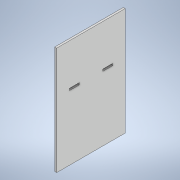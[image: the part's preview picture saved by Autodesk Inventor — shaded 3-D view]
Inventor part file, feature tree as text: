
AUTODESK INVENTOR PART (.ipt)
format: ipt  version: 2020 (Build 240168000, 168)  size: 120,832 bytes
history: native  units: mm
features: extrude x2, sketch x2
ambient origin geometry x8: Origin, YZ Plane, XZ Plane, XY Plane, X Axis, Y Axis, Z Axis, Center Point
bodies: Solid1 (feature_tree)
feature tree (4):
  extrude  "Extrusion1"  Depth=350.0mm
  extrude  "Extrusion3"  TaperAngle=0.0deg  [1 undecoded]
  sketch  "Sketch1"  dims[d0=550.0mm d1=350.0mm]
  sketch  "Sketch2"  dims[d2=175.0mm d3=0.0mm d4=10.0mm d5=0.0mm d6=50.0mm d7=60.0mm d15=10.0mm d16=0.0mm d18=210.0mm d19=10.0mm d20=10.0mm d22=10.0mm d23=10.0mm d24=50.0mm d25=210.0mm d26=60.0mm d9=0.5mm d10=0.872665mm d11=0.5mm d12=0.872665mm]
note: 1 required parameter value undecoded (feature->parameter linkage not recoverable at this tier; creation-order binding heuristic only, values carry confidence <= 0.55)
